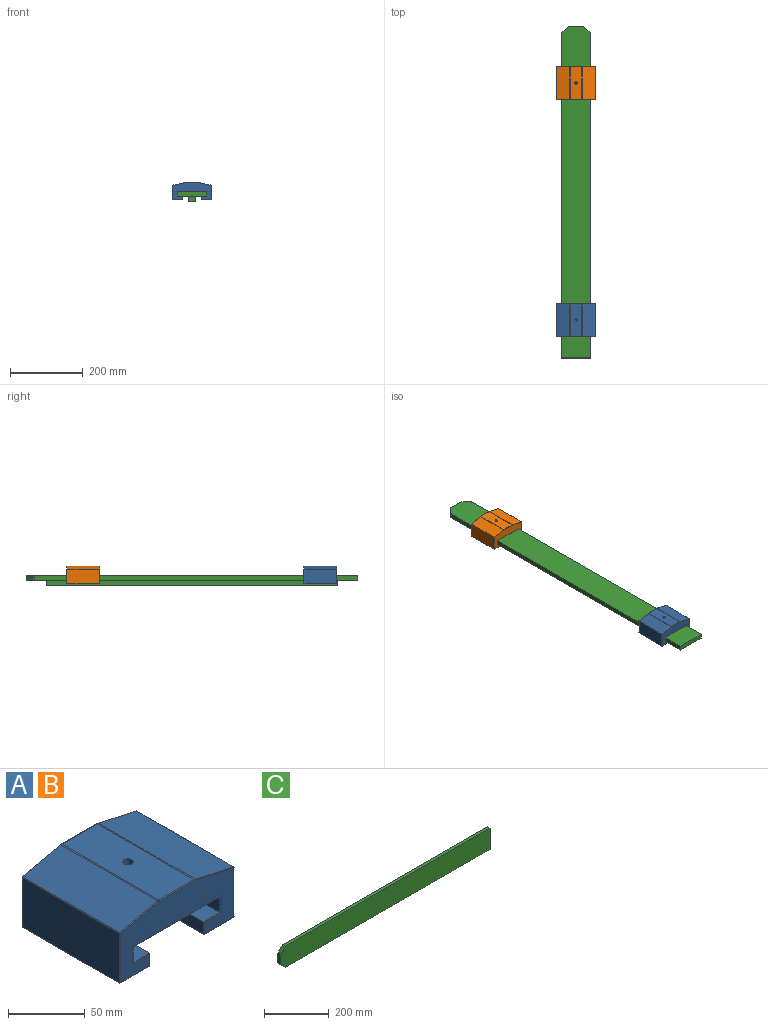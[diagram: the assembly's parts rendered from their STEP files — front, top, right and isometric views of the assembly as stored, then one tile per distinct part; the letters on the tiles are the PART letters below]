
ASSEMBLY  parts=3 mates=2
PART A: 71 faces, bbox 105.4x90x48 mm
  f0: plane 89x39.1mm, normal (1,0,0), area 3479.8mm2, adj f55,f56,f63,f64
  f1: plane 104.4x47mm, normal (0,-1,0), area 3062.6mm2, adj f25,f28,f29,f32,f33,f37,f44,f45
  f2: plane 89x39.1mm, normal (-1,0,0), area 3479.8mm2, adj f46,f47,f58,f59
  f3: plane 89x32.3mm, normal (0,0,1), area 2838.6mm2, adj f14,f19,f20,f41,f69
  f4: plane 89x27mm, normal (0,0,-1), area 2403mm2, adj f34,f35,f45,f46
  f5: plane 89x9.5mm, normal (1,0,0), area 845.5mm2, adj f6,f26,f33,f34
  f6: plane 89x15.3mm, normal (0,0,1), area 1361.7mm2, adj f5,f7,f23,f29
  f7: plane 89x12.7mm, normal (1,0,0), area 1130.3mm2, adj f6,f8,f21,f25
  f8: plane 89x80mm, normal (0,0,-1), area 6960.5mm2, adj f7,f9,f16,f22,f28
  f9: plane 89x12.7mm, normal (-1,0,0), area 1130.3mm2, adj f8,f10,f24,f32
  f10: plane 89x15.3mm, normal (0,0,1), area 1361.7mm2, adj f9,f11,f27,f37
  f11: plane 89x9.5mm, normal (-1,0,0), area 845.5mm2, adj f10,f31,f43,f44
  f12: plane 89x27mm, normal (0,0,-1), area 2403mm2, adj f42,f43,f56,f57
  f13: plane 104.4x47mm, normal (0,1,0), area 3062.6mm2, adj f21,f22,f23,f24,f26,f27,f31,f35
  f14: cylinder r=3.4mm len=17.3mm, axis (0,0,-1), area 369.6mm2, adj f3,f15
  f15: plane 14.25x14.25mm, normal (0,0,-1), area 123.2mm2, adj f14,f16
  f16: cylinder r=7.12mm len=14.25mm, axis (0,0,-1), area 358.1mm2, adj f8,f15
  f17: plane 89x35.07mm, normal (-0.22,0,0.98), area 3197.6mm2, adj f20,f48,f59,f65
  f18: plane 89x35.07mm, normal (0.22,0,0.98), area 3197.6mm2, adj f19,f54,f63,f68
  f19: cylinder r=5mm len=89mm, axis (0,-1,0), area 97.3mm2, adj f3,f18,f49,f70
  f20: cylinder r=5mm len=89mm, axis (0,-1,0), area 97.3mm2, adj f3,f17,f40,f67
  f21: cylinder r=0.5mm len=13.7mm, axis (0,0,1), area 10.3mm2, adj f7,f13,f22,f23
  f22: cylinder r=0.5mm len=81mm, axis (1,0,0), area 63.1mm2, adj f8,f13,f21,f24
  f23: cylinder r=0.5mm len=15.8mm, axis (-1,0,0), area 12mm2, adj f6,f13,f21,f26
  f24: cylinder r=0.5mm len=13.7mm, axis (0,0,-1), area 10.3mm2, adj f9,f13,f22,f27
  f25: cylinder r=0.5mm len=13.7mm, axis (0,0,-1), area 10.3mm2, adj f1,f7,f28,f29
  f26: cylinder r=0.5mm len=9.5mm, axis (0,0,1), area 7.3mm2, adj f5,f13,f23,f30
  f27: cylinder r=0.5mm len=15.8mm, axis (-1,0,0), area 12mm2, adj f10,f13,f24,f31
  f28: cylinder r=0.5mm len=81mm, axis (-1,0,0), area 63.1mm2, adj f1,f8,f25,f32
  f29: cylinder r=0.5mm len=15.8mm, axis (1,0,0), area 12mm2, adj f1,f6,f25,f33
  f30: sphere r=0.5mm, area 0.4mm2, adj f26,f34,f35
  f31: cylinder r=0.5mm len=9.5mm, axis (0,0,-1), area 7.3mm2, adj f11,f13,f27,f36
  f32: cylinder r=0.5mm len=13.7mm, axis (0,0,1), area 10.3mm2, adj f1,f9,f28,f37
  f33: cylinder r=0.5mm len=9.5mm, axis (0,0,-1), area 7.3mm2, adj f1,f5,f29,f38
  f34: cylinder r=0.5mm len=89mm, axis (0,1,0), area 69.9mm2, adj f4,f5,f30,f38
  f35: cylinder r=0.5mm len=27mm, axis (1,0,0), area 21.2mm2, adj f4,f13,f30,f39
  f36: sphere r=0.5mm, area 0.4mm2, adj f31,f42,f43
  f37: cylinder r=0.5mm len=15.8mm, axis (1,0,0), area 12mm2, adj f1,f10,f32,f44
  f38: sphere r=0.5mm, area 0.4mm2, adj f33,f34,f45
  f39: sphere r=0.5mm, area 0.4mm2, adj f35,f46,f47
  f40: torus R=4.5mm, axis (0,-1,0), area 0.8mm2, adj f13,f20,f41,f48
  f41: cylinder r=0.5mm len=32.3mm, axis (-1,0,0), area 25.4mm2, adj f3,f13,f40,f49
  f42: cylinder r=0.5mm len=27mm, axis (1,0,0), area 21.2mm2, adj f12,f13,f36,f50
  f43: cylinder r=0.5mm len=89mm, axis (0,-1,0), area 69.9mm2, adj f11,f12,f36,f51
  f44: cylinder r=0.5mm len=9.5mm, axis (0,0,1), area 7.3mm2, adj f1,f11,f37,f51
  f45: cylinder r=0.5mm len=27mm, axis (-1,0,0), area 21.2mm2, adj f1,f4,f38,f52
  f46: cylinder r=0.5mm len=89mm, axis (0,1,0), area 69.9mm2, adj f2,f4,f39,f52
  f47: cylinder r=0.5mm len=39.1mm, axis (0,0,-1), area 30.7mm2, adj f2,f13,f39,f53
  f48: cylinder r=0.5mm len=35.18mm, axis (-0.98,0,-0.22), area 28.2mm2, adj f13,f17,f40,f53
  f49: torus R=4.5mm, axis (0,-1,0), area 0.8mm2, adj f13,f19,f41,f54
  f50: sphere r=0.5mm, area 0.4mm2, adj f42,f55,f56
  f51: sphere r=0.5mm, area 0.4mm2, adj f43,f44,f57
  f52: sphere r=0.5mm, area 0.4mm2, adj f45,f46,f58
  f53: sphere r=0.5mm, area 0.3mm2, adj f47,f48,f59
  f54: cylinder r=0.5mm len=35.18mm, axis (-0.98,0,0.22), area 28.2mm2, adj f13,f18,f49,f60
  f55: cylinder r=0.5mm len=39.1mm, axis (0,0,1), area 30.7mm2, adj f0,f13,f50,f60
  f56: cylinder r=0.5mm len=89mm, axis (0,-1,0), area 69.9mm2, adj f0,f12,f50,f61
  f57: cylinder r=0.5mm len=27mm, axis (-1,0,0), area 21.2mm2, adj f1,f12,f51,f61
  f58: cylinder r=0.5mm len=39.1mm, axis (0,0,1), area 30.7mm2, adj f1,f2,f52,f62
  f59: cylinder r=0.5mm len=89mm, axis (0,1,0), area 60.2mm2, adj f2,f17,f53,f62
  f60: sphere r=0.5mm, area 0.3mm2, adj f54,f55,f63
  f61: sphere r=0.5mm, area 0.4mm2, adj f56,f57,f64
  f62: sphere r=0.5mm, area 0.3mm2, adj f58,f59,f65
  f63: cylinder r=0.5mm len=89mm, axis (0,-1,0), area 60.2mm2, adj f0,f18,f60,f66
  f64: cylinder r=0.5mm len=39.1mm, axis (0,0,-1), area 30.7mm2, adj f0,f1,f61,f66
  f65: cylinder r=0.5mm len=35.18mm, axis (-0.98,0,-0.22), area 28.2mm2, adj f1,f17,f62,f67
  f66: sphere r=0.5mm, area 0.3mm2, adj f63,f64,f68
  f67: torus R=4.5mm, axis (0,-1,0), area 0.8mm2, adj f1,f20,f65,f69
  f68: cylinder r=0.5mm len=35.18mm, axis (-0.98,0,0.22), area 28.2mm2, adj f1,f18,f66,f70
  f69: cylinder r=0.5mm len=32.3mm, axis (1,0,0), area 25.4mm2, adj f1,f3,f67,f70
  f70: torus R=4.5mm, axis (0,-1,0), area 0.8mm2, adj f1,f19,f68,f69
PART B: same geometry as A
PART C: 17 faces, bbox 910x27.7x80 mm
  f0: plane 887.93x12.7mm, normal (0,0,-1), area 11276.7mm2, adj f1,f4,f5,f13
  f1: plane 80x12.7mm, normal (1,0,0), area 1016mm2, adj f0,f2,f4,f5
  f2: plane 887.93x12.7mm, normal (0,0,1), area 11276.7mm2, adj f1,f4,f5,f14
  f3: plane 35.86x12.7mm, normal (-1,0,0), area 455.4mm2, adj f4,f5,f15,f16
  f4: plane 910x80mm, normal (0,-1,0), area 72397.8mm2, adj f0,f1,f2,f3,f11,f12,f13,f14
  f5: plane 910x80mm, normal (0,1,0), area 57197.8mm2, adj f0,f1,f2,f3,f6,f7,f8,f9
  f6: plane 800x15mm, normal (0,0,1), area 12000mm2, adj f5,f7,f9,f10
  f7: plane 19x15mm, normal (1,0,0), area 285mm2, adj f5,f6,f8,f10
  f8: plane 800x15mm, normal (0,0,-1), area 12000mm2, adj f5,f7,f9,f10
  f9: plane 19x15mm, normal (-1,0,0), area 285mm2, adj f5,f6,f8,f10
  f10: plane 800x19mm, normal (0,1,0), area 15200mm2, adj f6,f7,f8,f9
  f11: plane 17.07x17.07mm, normal (-0.71,0,0.71), area 306.6mm2, adj f4,f5,f14,f15
  f12: plane 17.07x17.07mm, normal (-0.71,0,-0.71), area 306.6mm2, adj f4,f5,f13,f16
  f13: cylinder r=5mm len=12.7mm, axis (0,1,0), area 49.9mm2, adj f0,f4,f5,f12
  f14: cylinder r=5mm len=12.7mm, axis (0,-1,0), area 49.9mm2, adj f2,f4,f5,f11
  f15: cylinder r=5mm len=12.7mm, axis (0,1,0), area 49.9mm2, adj f3,f4,f5,f11
  f16: cylinder r=5mm len=12.7mm, axis (0,1,0), area 49.9mm2, adj f3,f4,f5,f12
PLACE A t=(-98.28,-299.11,151.91)mm
PLACE B t=(-98.28,350.89,151.91)mm
PLACE C rot(axis=(-0.58,0.58,-0.58),120deg) t=(-98.28,7.38,139.21)mm
MATE planar C.f4 <-> A.f14  axis (0,0,1) through (-98.28,4.89,151.91)mm
MATE planar C.f4 <-> B.f14  axis (0,0,1) through (-98.28,4.89,151.91)mm
